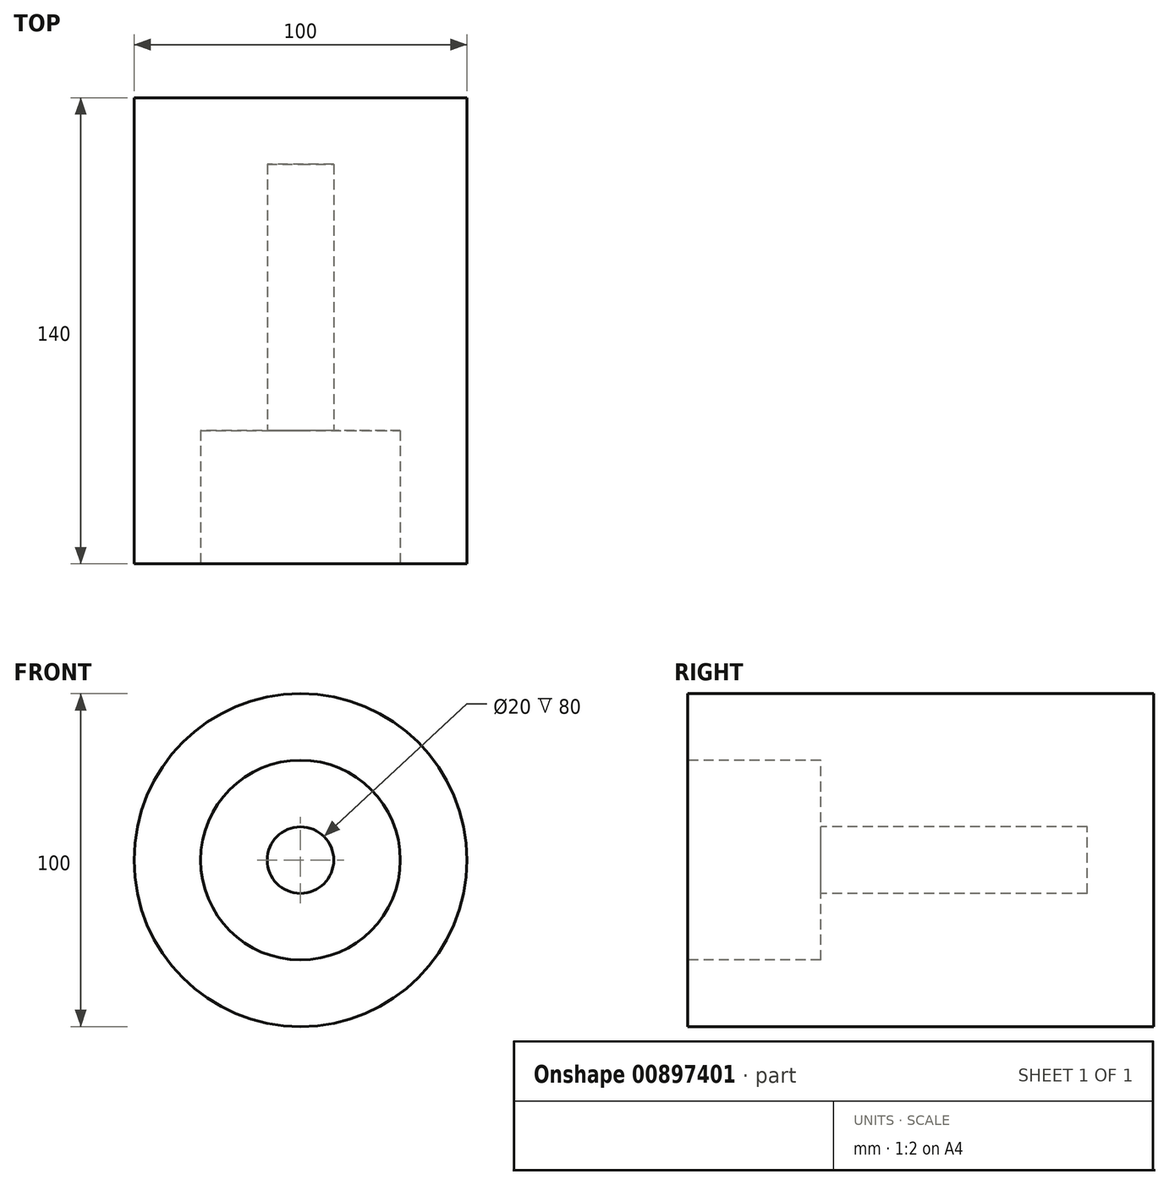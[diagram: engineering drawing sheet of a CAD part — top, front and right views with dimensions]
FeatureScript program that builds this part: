
annotation { "Feature Type Name" : "Feature", "Feature Type Description" : "" }
export const myFeature = defineFeature(function(context is Context, id is Id, definition is map)
    precondition{}
    {
        {
            var Q0;
            Q0=qCreatedBy(makeId("Front.planeOp"),FACE);
            var sketch = newSketch(context, id + "F0", { "sketchPlane" : qUnion([Q0])});
            skCircle(sketch, "E0", {"center": v(0, 0) * mm, "radius": 50 * mm});
            skSolve(sketch);
        }
        {
            var Q0;
            Q0 = qSketchRegion(id + "F0", true);
            extrude(context, id + "F1", {"entities" : qUnion([Q0]), "depth" : 70 * mm, "offsetDistance" : 25.4 * mm});
        }
        {
            var Q0;
            Q0=makeQuery(id+"F1.opExtrude","CAP_FACE",FACE,{"disambiguationData":[OSD([sQuery(id+"F0.wireOp",EDGE,"E0")])],"isStart":true});
            extrude(context, id + "F2", {"entities" : qUnion([Q0]), "operationType" : NewBodyOperationType.ADD, "depth" : 70 * mm, "offsetDistance" : 25.4 * mm});
        }
        {
            var Q0;
            Q0=makeQuery(id+"F1.opExtrude","CAP_FACE",FACE,{"disambiguationData":[OSD([sQuery(id+"F0.wireOp",EDGE,"E0")])],"isStart":false});
            var sketch = newSketch(context, id + "F3", { "sketchPlane" : qUnion([Q0])});
            skCircle(sketch, "E1", {"center": v(0, 0) * mm, "radius": 30 * mm});
            skSolve(sketch);
        }
        {
            var Q0;
            Q0 = qSketchRegion(id + "F3", true);
            extrude(context, id + "F4", {"entities" : qUnion([Q0]), "operationType" : NewBodyOperationType.REMOVE, "oppositeDirection" : true, "depth" : 40 * mm, "offsetDistance" : 25.4 * mm});
        }
        {
            var Q0;
            Q0=makeQuery(id+"F4.boolean.opBoolean","COPY",FACE,{"derivedFrom":makeQuery(id+"F4.opExtrude","CAP_FACE",FACE,{"disambiguationData":[OSD([sQuery(id+"F3.wireOp",EDGE,"E1")])],"isStart":false})});
            var sketch = newSketch(context, id + "F5", { "sketchPlane" : qUnion([Q0])});
            skCircle(sketch, "E2", {"center": v(0, 0) * mm, "radius": 10 * mm});
            skSolve(sketch);
        }
        {
            var Q0;
            Q0=makeQuery(id+"F5.imprint","IMPRINT",FACE,{"disambiguationData":[TD([[makeQuery(id+"F5.imprint","IMPRINT",EDGE,{"derivedFrom":sQuery(id+"F5.wireOp",EDGE,"E2")}),1.0]])]});
            extrude(context, id + "F6", {"entities" : qUnion([Q0]), "operationType" : NewBodyOperationType.REMOVE, "oppositeDirection" : true, "depth" : 80 * mm, "offsetDistance" : 25.4 * mm});
        }
    });
